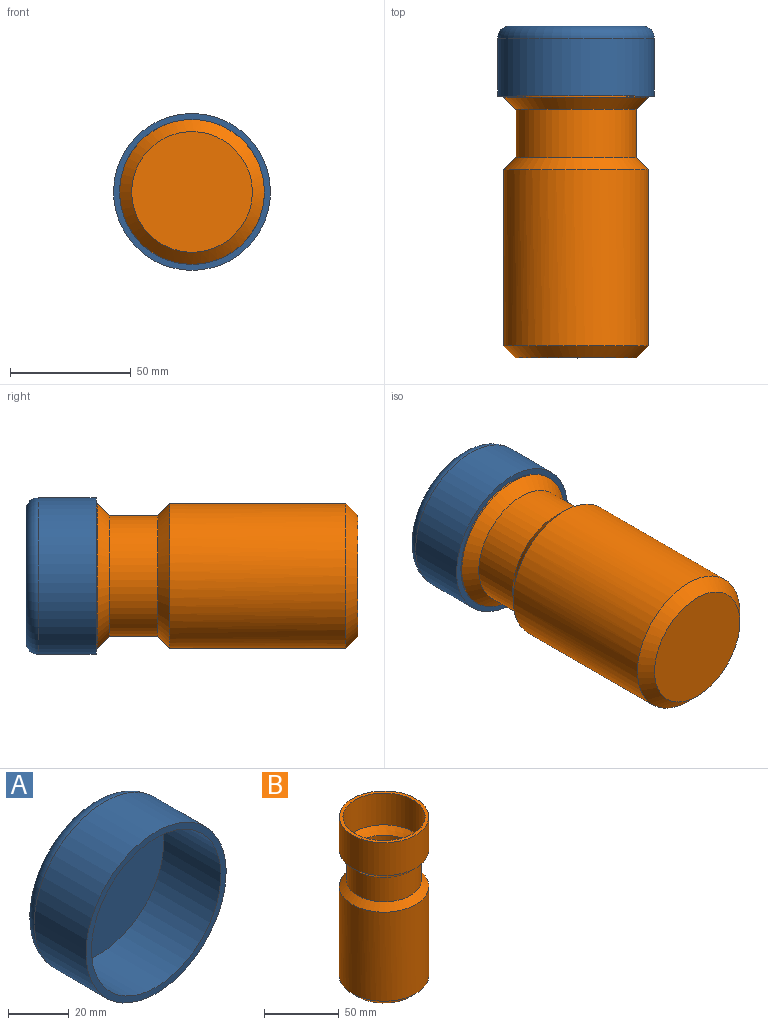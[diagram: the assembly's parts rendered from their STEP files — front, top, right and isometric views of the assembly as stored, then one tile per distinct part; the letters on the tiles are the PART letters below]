
ASSEMBLY  parts=2 mates=1
PART A: 6 faces, bbox 70.4x29x70.4 mm
  f0: cylinder r=32.5mm len=65mm, axis (0,1,0), area 4900.9mm2, adj f1,f5
  f1: plane 65x65mm, normal (0,-1,0), area 490.9mm2, adj f0,f3
  f2: plane 55x55mm, normal (0,1,0), area 2375.8mm2, adj f5
  f3: cylinder r=30mm len=60mm, axis (0,1,0), area 4995.1mm2, adj f1,f4
  f4: plane 60x60mm, normal (0,-1,0), area 2827.4mm2, adj f3
  f5: torus R=27.5mm, axis (0,-1,0), area 1514.2mm2, adj f0,f2
PART B: 15 faces, bbox 60x60x135 mm
  f0: plane 60x60mm, normal (0,0,1), area 451.6mm2, adj f4,f11
  f1: plane 50x50mm, normal (0,0,-1), area 1963.5mm2, adj f7
  f2: cylinder r=30mm len=73mm, axis (0,0,1), area 13760.2mm2, adj f6,f7
  f3: cylinder r=25mm len=50mm, axis (0,0,1), area 3141.6mm2, adj f5,f6
  f4: cylinder r=30mm len=60mm, axis (0,0,1), area 5089.4mm2, adj f0,f5
  f5: cone r=30mm half-angle=45deg, axis (0,0,1), area 1221.8mm2, adj f3,f4
  f6: cone r=25mm half-angle=45deg, axis (0,0,-1), area 1221.8mm2, adj f2,f3
  f7: cone r=30mm half-angle=45deg, axis (0,0,1), area 1221.8mm2, adj f1,f2
  f8: plane 47.93x47.93mm, normal (0,0,1), area 1804.2mm2, adj f14
  f9: cylinder r=27.5mm len=70.93mm, axis (0,0,1), area 12255.6mm2, adj f13,f14
  f10: cylinder r=22.5mm len=45mm, axis (0,0,1), area 3120.2mm2, adj f12,f13
  f11: cylinder r=27.5mm len=55mm, axis (0,0,1), area 4486.3mm2, adj f0,f12
  f12: cone r=28.23mm half-angle=45deg, axis (0,0,1), area 1110.7mm2, adj f10,f11
  f13: cone r=23.23mm half-angle=45deg, axis (0,0,-1), area 1110.7mm2, adj f9,f10
  f14: cone r=28.23mm half-angle=45deg, axis (0,0,1), area 808.4mm2, adj f8,f9
PLACE A t=(-48.62,-32.39,57.77)mm
PLACE B rot(axis=(-1,0,0),90deg) t=(-48.62,-119.89,57.77)mm
MATE fastened B.f2 <-> A.f0  axis (0,1,0) through (-48.62,-34.89,57.77)mm
